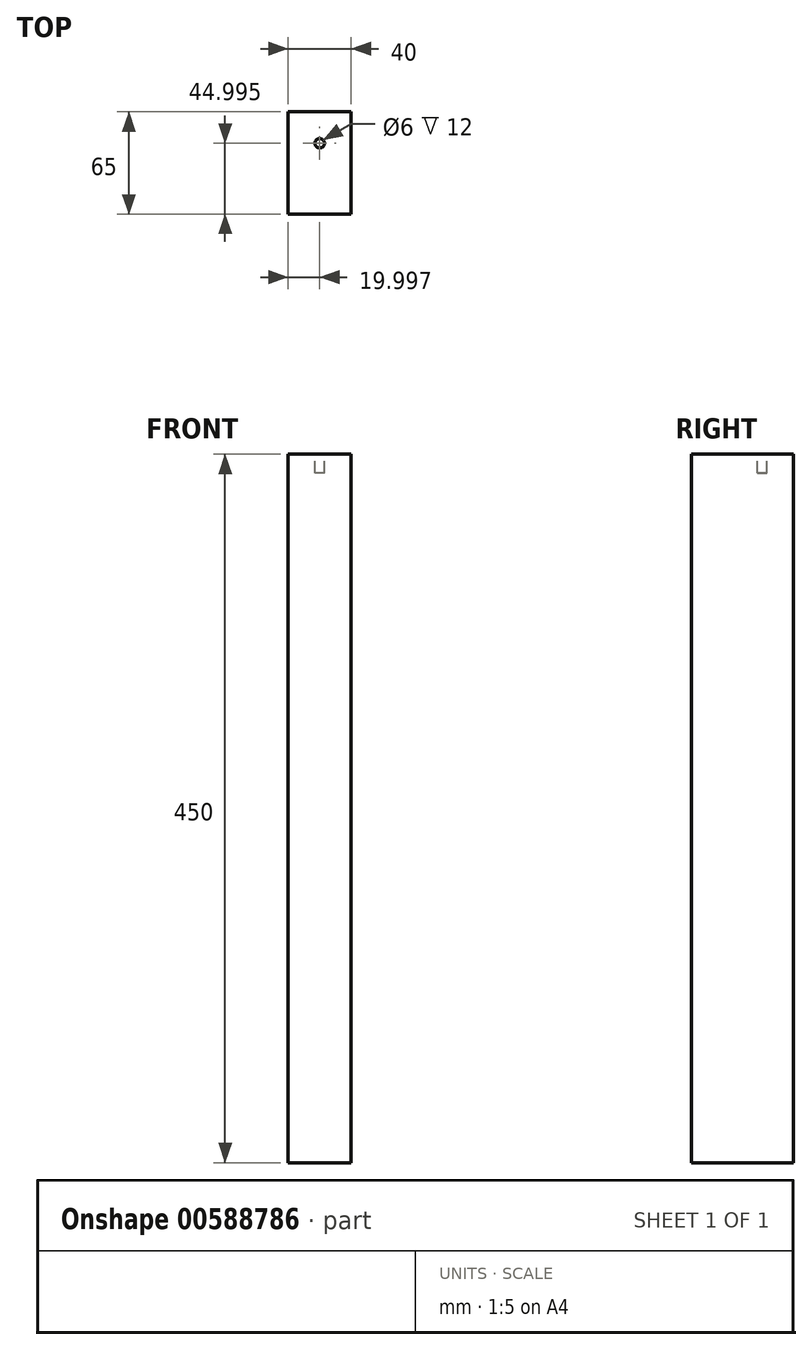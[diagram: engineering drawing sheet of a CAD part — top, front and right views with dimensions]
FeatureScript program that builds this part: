
annotation { "Feature Type Name" : "Feature", "Feature Type Description" : "" }
export const myFeature = defineFeature(function(context is Context, id is Id, definition is map)
    precondition{}
    {
        {
            var Q0;
            Q0=qCreatedBy(makeId("Top.planeOp"),FACE);
            var sketch = newSketch(context, id + "F0", { "sketchPlane" : qUnion([Q0])});
            skLineSegment(sketch, "E0.bottom", {"start": v(-16.68, 8.16) * mm, "end": v(23.32, 8.16) * mm});
            skLineSegment(sketch, "E0.top", {"start": v(-16.68, -31.84) * mm, "end": v(23.32, -31.84) * mm});
            skLineSegment(sketch, "E0.left", {"start": v(-16.68, 8.16) * mm, "end": v(-16.68, -31.84) * mm});
            skLineSegment(sketch, "E0.right", {"start": v(23.32, 8.16) * mm, "end": v(23.32, -31.84) * mm});
            skSolve(sketch);
        }
        {
            var Q0;
            Q0=makeQuery(id+"F0.imprint","IMPRINT",FACE,{"disambiguationData":[TD([[makeQuery(id+"F0.imprint","IMPRINT",EDGE,{"derivedFrom":sQuery(id+"F0.wireOp",EDGE,"E0.bottom")}),-1.0]])]});
            extrude(context, id + "F1", {"entities" : qUnion([Q0]), "depth" : 450 * mm, "offsetDistance" : 25 * mm});
        }
        {
            var Q0;
            Q0=makeQuery(id+"F1.opExtrude","CAP_FACE",FACE,{"disambiguationData":[OSD([sQuery(id+"F0.wireOp",EDGE,"E0.bottom"),sQuery(id+"F0.wireOp",EDGE,"E0.top"),sQuery(id+"F0.wireOp",EDGE,"E0.left"),sQuery(id+"F0.wireOp",EDGE,"E0.right")])],"isStart":false});
            var sketch = newSketch(context, id + "F2", { "sketchPlane" : qUnion([Q0])});
            skCircle(sketch, "E1", {"center": v(3.32, -11.84) * mm, "radius": 5 * mm});
            skPoint(sketch, "E1.centerSnap0", {"position": v(23.32, -11.84) * mm});
            skPoint(sketch, "E1.centerSnap1", {"position": v(3.32, 8.16) * mm});
            skSolve(sketch);
        }
        {
            var Q0;
            Q0=makeQuery(id+"F2.imprint","IMPRINT",FACE,{"disambiguationData":[TD([[makeQuery(id+"F2.imprint","IMPRINT",EDGE,{"derivedFrom":sQuery(id+"F2.wireOp",EDGE,"E1")}),1.0]])]});
            extrude(context, id + "F3", {"entities" : qUnion([Q0]), "operationType" : NewBodyOperationType.ADD, "depth" : 10 * mm, "offsetDistance" : 25 * mm});
        }
        {
            var Q0;
            Q0=makeQuery(id+"F3.opExtrude","CAP_FACE",FACE,{"disambiguationData":[OSD([sQuery(id+"F2.wireOp",EDGE,"E1")])],"isStart":false});
            extrude(context, id + "F4", {"entities" : qUnion([Q0]), "operationType" : NewBodyOperationType.REMOVE, "oppositeDirection" : true, "depth" : 10 * mm, "offsetDistance" : 25 * mm});
        }
        {
            var Q0;
            Q0=makeQuery(id+"F4.boolean.opBoolean","MERGE",FACE,{"derivedFrom":[makeQuery(id+"F1.opExtrude","CAP_FACE",FACE,{"disambiguationData":[OSD([sQuery(id+"F0.wireOp",EDGE,"E0.bottom"),sQuery(id+"F0.wireOp",EDGE,"E0.top"),sQuery(id+"F0.wireOp",EDGE,"E0.left"),sQuery(id+"F0.wireOp",EDGE,"E0.right")])],"isStart":false}),makeQuery(id+"F4.opExtrude","CAP_FACE",FACE,{"disambiguationData":[OSD([sQuery(id+"F2.wireOp",EDGE,"E1")])],"isStart":false})]});
            var sketch = newSketch(context, id + "F5", { "sketchPlane" : qUnion([Q0])});
            skCircle(sketch, "E2", {"center": v(3.32, -11.84) * mm, "radius": 3 * mm});
            skPoint(sketch, "E2.centerSnap0", {"position": v(3.32, 8.16) * mm});
            skPoint(sketch, "E2.centerSnap1", {"position": v(23.32, -11.84) * mm});
            skSolve(sketch);
        }
        {
            var Q0;
            Q0=makeQuery(id+"F5.imprint","IMPRINT",FACE,{"disambiguationData":[TD([[makeQuery(id+"F5.imprint","IMPRINT",EDGE,{"derivedFrom":sQuery(id+"F5.wireOp",EDGE,"E2")}),1.0]])]});
            extrude(context, id + "F6", {"entities" : qUnion([Q0]), "operationType" : NewBodyOperationType.REMOVE, "oppositeDirection" : true, "depth" : 12 * mm, "offsetDistance" : 25 * mm});
        }
        {
            var Q0;
            Q0=makeQuery(id+"F1.opExtrude","SWEPT_FACE",FACE,{"disambiguationData":[OSD([sQuery(id+"F0.wireOp",EDGE,"E0.top")])]});
            extrude(context, id + "F7", {"entities" : qUnion([Q0]), "operationType" : NewBodyOperationType.ADD, "depth" : 25 * mm, "offsetDistance" : 25 * mm});
        }
    });
